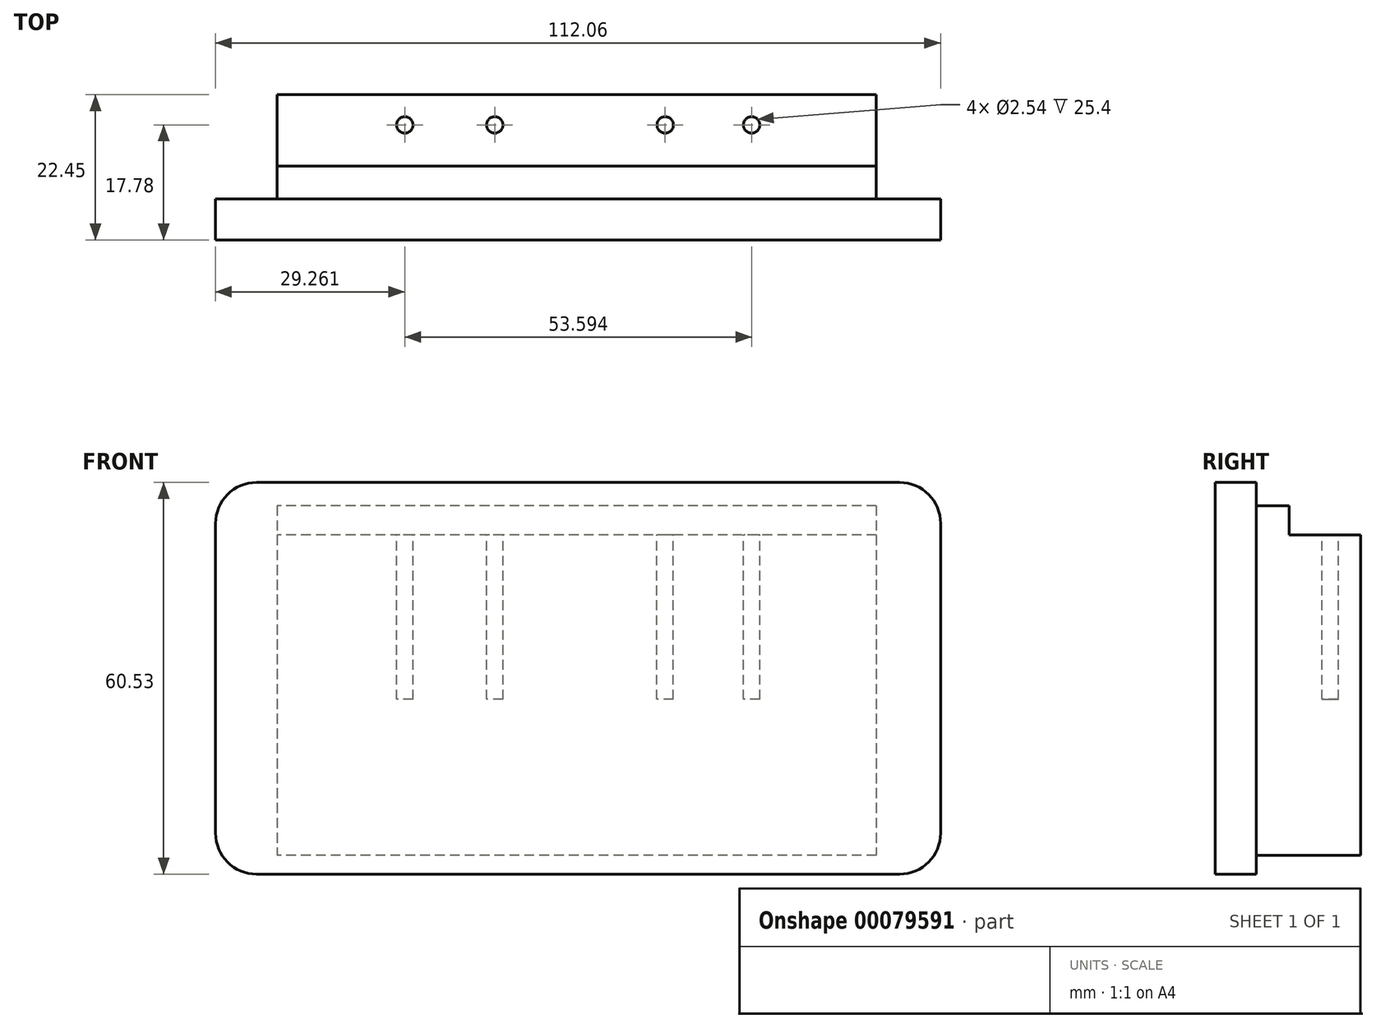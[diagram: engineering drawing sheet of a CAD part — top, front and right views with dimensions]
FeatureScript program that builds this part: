
annotation { "Feature Type Name" : "Feature", "Feature Type Description" : "" }
export const myFeature = defineFeature(function(context is Context, id is Id, definition is map)
    precondition{}
    {
        {
            var Q0;
            Q0=qCreatedBy(makeId("Front.planeOp"),FACE);
            var sketch = newSketch(context, id + "F0", { "sketchPlane" : qUnion([Q0])});
            skLineSegment(sketch, "E0.bottom", {"start": v(6.35, 0) * mm, "end": v(105.71, 0) * mm});
            skLineSegment(sketch, "E0.top", {"start": v(6.35, 60.53) * mm, "end": v(105.71, 60.53) * mm});
            skLineSegment(sketch, "E0.left", {"start": v(0, 6.35) * mm, "end": v(0, 54.18) * mm});
            skLineSegment(sketch, "E0.right", {"start": v(112.06, 6.35) * mm, "end": v(112.06, 54.18) * mm});
            skPoint(sketch, "E1.visualSharp", {"position": v(0, 60.53) * mm});
            skArc(sketch, "E1.filletArc", {"start": v(6.35, 60.53) * mm, "mid": v(1.86, 58.67) * mm, "end": v(0, 54.18) * mm});
            skPoint(sketch, "E2.visualSharp", {"position": v(0, 0) * mm});
            skArc(sketch, "E2.filletArc", {"start": v(0, 6.35) * mm, "mid": v(1.86, 1.86) * mm, "end": v(6.35, 0) * mm});
            skPoint(sketch, "E3.visualSharp", {"position": v(112.06, 0) * mm});
            skArc(sketch, "E3.filletArc", {"start": v(105.71, 0) * mm, "mid": v(110.2, 1.86) * mm, "end": v(112.06, 6.35) * mm});
            skPoint(sketch, "E4.visualSharp", {"position": v(112.06, 60.53) * mm});
            skArc(sketch, "E4.filletArc", {"start": v(112.06, 54.18) * mm, "mid": v(110.2, 58.67) * mm, "end": v(105.71, 60.53) * mm});
            skSolve(sketch);
        }
        {
            var Q0;
            Q0=makeQuery(id+"F0.imprint","IMPRINT",FACE,{"disambiguationData":[TD([[makeQuery(id+"F0.imprint","IMPRINT",EDGE,{"derivedFrom":sQuery(id+"F0.wireOp",EDGE,"E0.bottom")}),1.0]])]});
            extrude(context, id + "F1", {"entities" : qUnion([Q0]), "oppositeDirection" : true, "depth" : 6.35 * mm});
        }
        {
            var Q0;
            Q0=makeQuery(id+"F1.opExtrude","CAP_FACE",FACE,{"disambiguationData":[OSD([sQuery(id+"F0.wireOp",EDGE,"E0.bottom"),sQuery(id+"F0.wireOp",EDGE,"E0.top"),sQuery(id+"F0.wireOp",EDGE,"E0.left"),sQuery(id+"F0.wireOp",EDGE,"E0.right"),sQuery(id+"F0.wireOp",EDGE,"E1.filletArc"),sQuery(id+"F0.wireOp",EDGE,"E2.filletArc"),sQuery(id+"F0.wireOp",EDGE,"E3.filletArc"),sQuery(id+"F0.wireOp",EDGE,"E4.filletArc")])],"isStart":false});
            var sketch = newSketch(context, id + "F2", { "sketchPlane" : qUnion([Q0])});
            skLineSegment(sketch, "E5.bottom", {"start": v(-102.13, 56.92) * mm, "end": v(-9.5, 56.92) * mm});
            skLineSegment(sketch, "E5.top", {"start": v(-102.13, 2.92) * mm, "end": v(-9.5, 2.92) * mm});
            skLineSegment(sketch, "E5.left", {"start": v(-102.13, 56.92) * mm, "end": v(-102.13, 2.92) * mm});
            skLineSegment(sketch, "E5.right", {"start": v(-9.5, 56.92) * mm, "end": v(-9.5, 2.92) * mm});
            skSolve(sketch);
        }
        {
            var Q0;
            Q0=makeQuery(id+"F2.imprint","IMPRINT",FACE,{"disambiguationData":[TD([[makeQuery(id+"F2.imprint","IMPRINT",EDGE,{"derivedFrom":sQuery(id+"F2.wireOp",EDGE,"E5.bottom")}),-1.0]])]});
            extrude(context, id + "F3", {"entities" : qUnion([Q0]), "operationType" : NewBodyOperationType.ADD, "depth" : 5.08 * mm});
        }
        {
            var Q0;
            Q0=makeQuery(id+"F3.opExtrude","CAP_FACE",FACE,{"disambiguationData":[OSD([sQuery(id+"F2.wireOp",EDGE,"E5.bottom"),sQuery(id+"F2.wireOp",EDGE,"E5.top"),sQuery(id+"F2.wireOp",EDGE,"E5.left"),sQuery(id+"F2.wireOp",EDGE,"E5.right")])],"isStart":false});
            var sketch = newSketch(context, id + "F4", { "sketchPlane" : qUnion([Q0])});
            skLineSegment(sketch, "E6.bottom", {"start": v(-102.13, 52.4) * mm, "end": v(-9.5, 52.4) * mm});
            skLineSegment(sketch, "E6.top", {"start": v(-102.13, 2.92) * mm, "end": v(-9.5, 2.92) * mm});
            skLineSegment(sketch, "E6.left", {"start": v(-102.13, 52.4) * mm, "end": v(-102.13, 2.92) * mm});
            skLineSegment(sketch, "E6.right", {"start": v(-9.5, 52.4) * mm, "end": v(-9.5, 2.92) * mm});
            skSolve(sketch);
        }
        {
            var Q0;
            Q0=makeQuery(id+"F4.imprint","IMPRINT",FACE,{"disambiguationData":[TD([[makeQuery(id+"F4.imprint","IMPRINT",EDGE,{"derivedFrom":sQuery(id+"F4.wireOp",EDGE,"E6.bottom")}),-1.0]])]});
            extrude(context, id + "F5", {"entities" : qUnion([Q0]), "operationType" : NewBodyOperationType.ADD, "depth" : 11.02 * mm});
        }
        {
            var Q0;
            Q0=makeQuery(id+"F5.opExtrude","SWEPT_FACE",FACE,{"disambiguationData":[OSD([sQuery(id+"F4.wireOp",EDGE,"E6.bottom")])]});
            var sketch = newSketch(context, id + "F6", { "sketchPlane" : qUnion([Q0])});
            skCircle(sketch, "E7", {"center": v(82.85, 17.78) * mm, "radius": 1.27 * mm});
            skCircle(sketch, "E8", {"center": v(69.5, 17.78) * mm, "radius": 1.27 * mm});
            skCircle(sketch, "E9", {"center": v(43.15, 17.78) * mm, "radius": 1.27 * mm});
            skCircle(sketch, "E10", {"center": v(29.26, 17.78) * mm, "radius": 1.27 * mm});
            skSolve(sketch);
        }
        {
            var Q0;
            Q0=makeQuery(id+"F6.imprint","IMPRINT",FACE,{"disambiguationData":[TD([[makeQuery(id+"F6.imprint","IMPRINT",EDGE,{"derivedFrom":sQuery(id+"F6.wireOp",EDGE,"E10")}),1.0]])]});
            var Q1;
            Q1=makeQuery(id+"F6.imprint","IMPRINT",FACE,{"disambiguationData":[TD([[makeQuery(id+"F6.imprint","IMPRINT",EDGE,{"derivedFrom":sQuery(id+"F6.wireOp",EDGE,"E9")}),1.0]])]});
            var Q2;
            Q2=makeQuery(id+"F6.imprint","IMPRINT",FACE,{"disambiguationData":[TD([[makeQuery(id+"F6.imprint","IMPRINT",EDGE,{"derivedFrom":sQuery(id+"F6.wireOp",EDGE,"E8")}),1.0]])]});
            var Q3;
            Q3=makeQuery(id+"F6.imprint","IMPRINT",FACE,{"disambiguationData":[TD([[makeQuery(id+"F6.imprint","IMPRINT",EDGE,{"derivedFrom":sQuery(id+"F6.wireOp",EDGE,"E7")}),1.0]])]});
            extrude(context, id + "F7", {"entities" : qUnion([Q0, Q1, Q2, Q3]), "operationType" : NewBodyOperationType.REMOVE, "oppositeDirection" : true, "depth" : 25.4 * mm});
        }
    });
